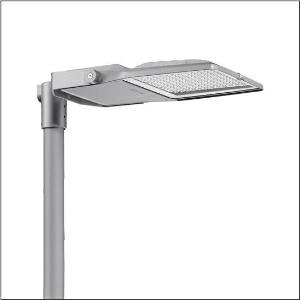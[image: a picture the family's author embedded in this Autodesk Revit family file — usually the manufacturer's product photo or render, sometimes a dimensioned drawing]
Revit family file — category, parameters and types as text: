
# Revit family: floodlight_fl_21_midi___pl52_5xa7785e2d3a_ba97
name_source: partatom
category: Lighting Fixtures
units: mm (PartAtom-declared; Revit-internal decimal feet)

## family parameters
Cut with Voids When Loaded = No
Host = Face
Light Source = No
Part Type = Normal
Room Calculation Point = No
Round Connector Dimension = Use Diameter
Shared = No

## types (1)
- --- (1 x LED, 26940 lm, 212.4 W, 3000K)
    Apparent Load = 212 VA
    CIE Flux Codes = 26 60 98 100 100
    Color Rendering = 70
    Color Temperature = 3000K
    Default Elevation = 1800 mm
    Description = Floodlight FL 21 midi, floodlight, primary light control with lens, of PMMA, primary optical cover: protective disc, of toughened safety glass, transparent, light distribution: PL52, light emission: direct distribution, installation type: surface-mounted, LED, High Power LED, rated luminous flux: 26.940lm, luminous efficacy: 127lm/W, light colour: 730, colour temperature: 3000K, control gear: Smart Interface (Zhaga), control: flexible luminous flux parameterisation, time-dependent luminous flux control, constant luminous flux control, overheat protection, pre-setting: logarithmic dimming characteristic, with terminal, 6-pole, mains connection: 220..240V, AC, 50/60Hz, start of lifetime: 212W, end of service life: 231W, reduction: 95W, luminaire housing, of diecast aluminium, powder-coated, SITECO metallic grey (DB 702S), corrosivity category C5 mid according to DIN EN ISO 12944, suitable for swimming pools, chlorine-resistant, sealing non-destructively replaceable, please order mast flange separately, mast bracket, of steel, galvanised, powder-coated, SITECO metallic grey (DB 702S), Smart Interface above, protection rating (complete): IP66, insulation class (complete): insulation class II (safety insulation), certification: CE, ENEC, VDE, protection symbol: D, impact resistance: IK08, permissible operating ambient temperature: -20..+40°C, permissible operating ambient temperature for outdoor applications: -40..+50°C, standard: DIN EN 12944, LABS conformity tested according to VDMA 24364:2018-05, packaging unit: 1 piece

Light Distribution: PL52
    Height = 76 mm
    Lamp = 1 x LED
    Lamp Light Flux = 26940 lm
    Lamp Power = 212.4 W
    Lamp count = 1
    Length = 657 mm
    Luminous efficacy = 127 lm/W
    Manufacturer = Siteco
    ModVariant = No
    Model = 5XA7785E2D3A
    Mounting Place = Pole
    Mounting Type = Pole annexe
    Number of Poles = 1
    OnlyDefault = Yes
    Power Factor = 1
    Product Name = Floodlight FL 21 midi | PL52
    Product group = floodlight | pylon annexe
    ProductGroupID = 6201
    Protection Class = Protection class II
    Protection Degree = IP 66
    RLX_Detail_Level = 1
    RLX_Emergency_Light_Flux = 0 lm
    RLX_Emergency_Type = 0
    RLX_Emergency_Type_DB = No
    RlxData = <blob elided: 153953 chars, md5=a778de75>
    Socket = socket
    Standby Power = 0 W
    System Light Flux = 26940 lm
    System Power = 212 W
    Type Comments = factory setting: luminous flux: 100 % | dim-lin: 254 | 710 mA
    Type Image = l_1007123.jpg
    URL = http://relux.com
    VarID = @adj_178667
    Voltage = 0 V
    Weight = 0.00 kg
    Width = 442 mm

## geometry (parser evidence)
native form markers: Blend x4, Sweep x12
no freeform markers — native parametric forms only
